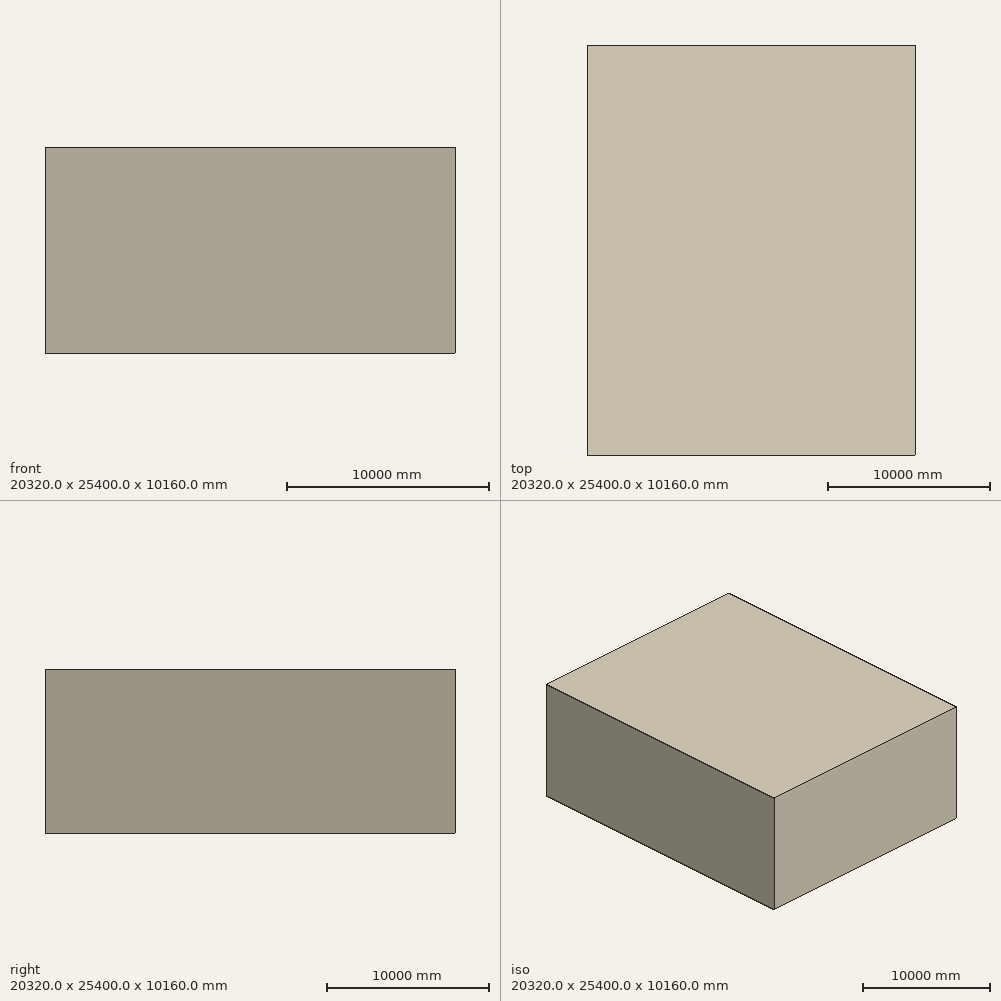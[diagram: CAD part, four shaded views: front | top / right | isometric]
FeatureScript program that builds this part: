
annotation { "Feature Type Name" : "Feature", "Feature Type Description" : "" }
export const myFeature = defineFeature(function(context is Context, id is Id, definition is map)
    precondition{}
    {
        {
            var Q0;
            Q0=qCreatedBy(makeId("Front.planeOp"),FACE);
            var sketch = newSketch(context, id + "F0", { "sketchPlane" : qUnion([Q0])});
            skLineSegment(sketch, "E0.bottom", {"start": v(0, 0) * mm, "end": v(20320, 0) * mm});
            skLineSegment(sketch, "E0.top", {"start": v(0, 10160) * mm, "end": v(20320, 10160) * mm});
            skLineSegment(sketch, "E0.left", {"start": v(0, 0) * mm, "end": v(0, 10160) * mm});
            skLineSegment(sketch, "E0.right", {"start": v(20320, 0) * mm, "end": v(20320, 10160) * mm});
            skSolve(sketch);
        }
        {
            var Q0;
            Q0=makeQuery(id+"F0.imprint","IMPRINT",FACE,{"disambiguationData":[TD([[makeQuery(id+"F0.imprint","IMPRINT",EDGE,{"derivedFrom":sQuery(id+"F0.wireOp",EDGE,"E0.bottom")}),1.0]])]});
            extrude(context, id + "F1", {"entities" : qUnion([Q0]), "depth" : 25400 * mm});
        }
    });
